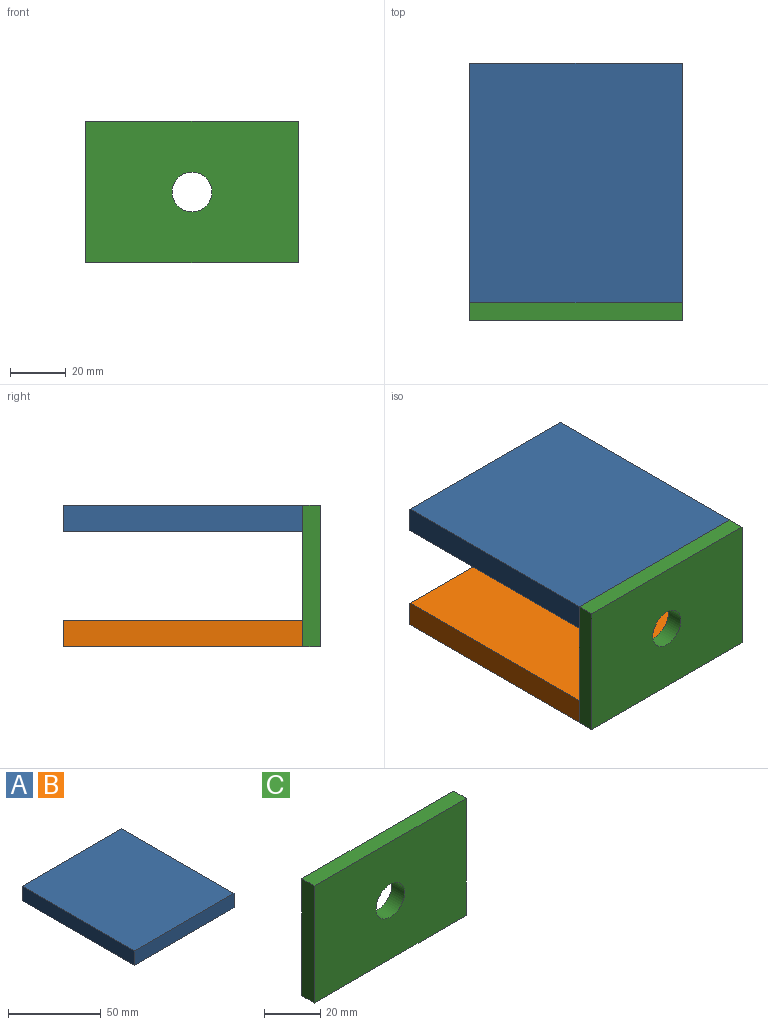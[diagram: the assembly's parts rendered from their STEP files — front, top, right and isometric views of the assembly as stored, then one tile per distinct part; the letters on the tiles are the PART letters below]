
ASSEMBLY  parts=3 mates=1
PART A: 6 faces, bbox 76.2x85.7x9.5 mm
  f0: plane 85.73x9.53mm, normal (1,0,0), area 816.5mm2, adj f1,f3,f4,f5
  f1: plane 76.2x9.53mm, normal (0,1,0), area 725.8mm2, adj f0,f2,f4,f5
  f2: plane 85.73x9.53mm, normal (-1,0,0), area 816.5mm2, adj f1,f3,f4,f5
  f3: plane 76.2x9.53mm, normal (0,-1,0), area 725.8mm2, adj f0,f2,f4,f5
  f4: plane 85.73x76.2mm, normal (0,0,-1), area 6532.2mm2, adj f0,f1,f2,f3
  f5: plane 85.73x76.2mm, normal (0,0,1), area 6532.2mm2, adj f0,f1,f2,f3
PART B: same geometry as A
PART C: 7 faces, bbox 76.2x6.4x50.8 mm
  f0: plane 76.2x6.35mm, normal (0,0,-1), area 483.9mm2, adj f1,f2,f3,f4
  f1: plane 50.8x6.35mm, normal (-1,0,0), area 322.6mm2, adj f0,f2,f4,f5
  f2: plane 76.2x50.8mm, normal (0,-1,0), area 3710.6mm2, adj f0,f1,f3,f5,f6
  f3: plane 50.8x6.35mm, normal (1,0,0), area 322.6mm2, adj f0,f2,f4,f5
  f4: plane 76.2x50.8mm, normal (0,1,0), area 3710.6mm2, adj f0,f1,f3,f5,f6
  f5: plane 76.2x6.35mm, normal (0,0,1), area 483.9mm2, adj f1,f2,f3,f4
  f6: cylinder r=7.14mm len=14.29mm, axis (0,-1,0), area 285mm2, adj f2,f4
PLACE A at identity
PLACE B rot(axis=(0,-1,0),180deg) t=(-2463.8,0,10109.2)mm
PLACE C at identity
MATE fastened C.f5 <-> A.f5  axis (0,0,1) through (-1231.9,-838.2,5080)mm
